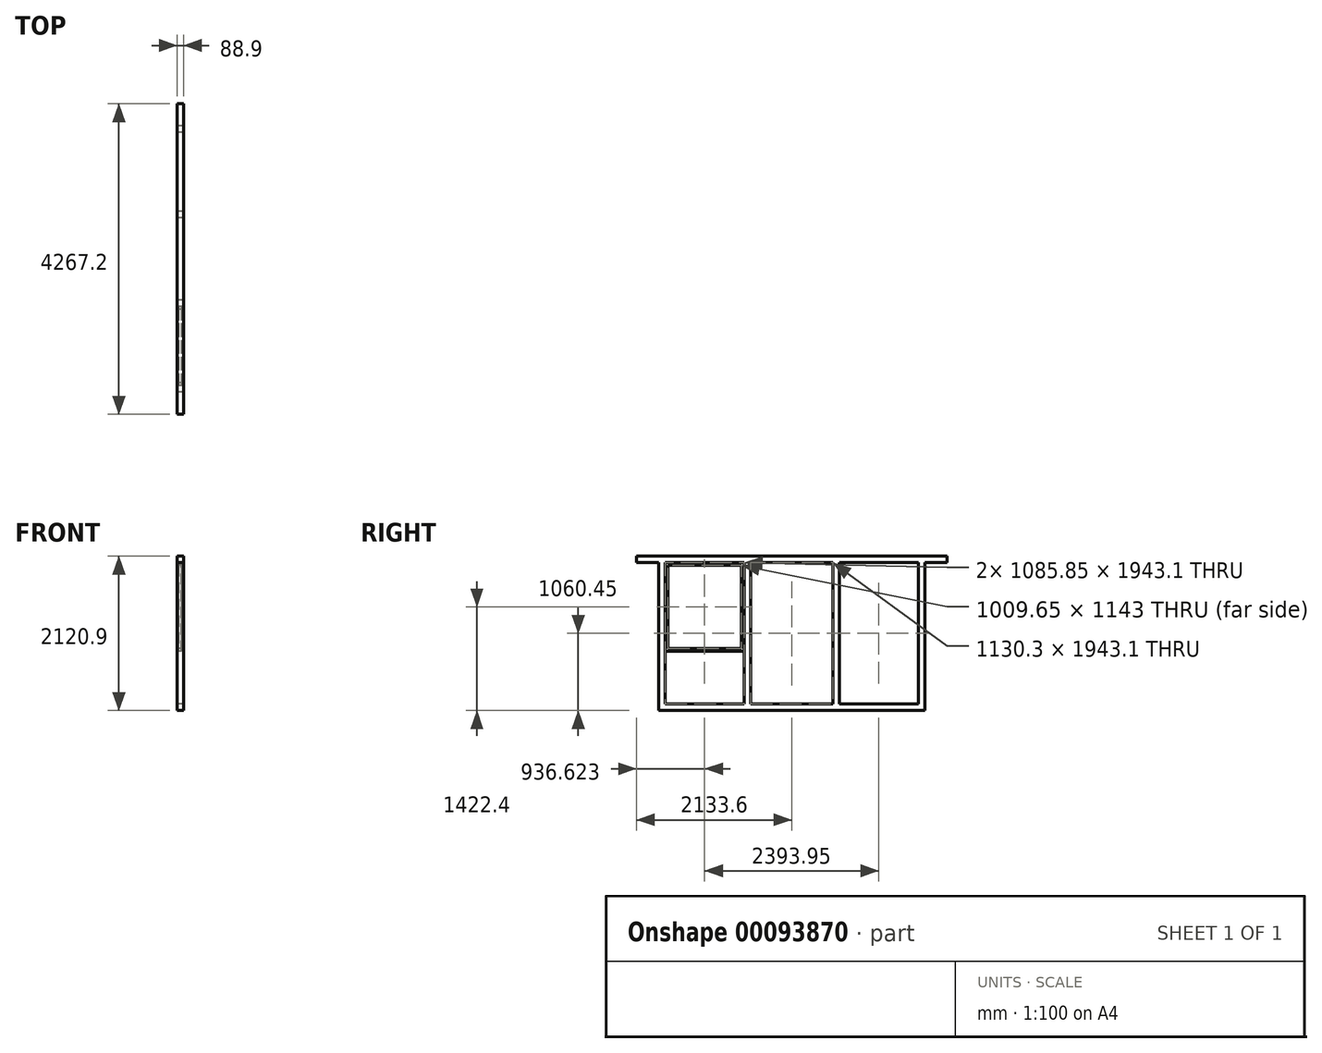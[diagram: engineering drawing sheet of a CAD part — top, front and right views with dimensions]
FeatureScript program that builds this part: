
annotation { "Feature Type Name" : "Feature", "Feature Type Description" : "" }
export const myFeature = defineFeature(function(context is Context, id is Id, definition is map)
    precondition{}
    {
        {
            var Q0;
            Q0=qCreatedBy(makeId("Right.planeOp"),FACE);
            var sketch = newSketch(context, id + "F0", { "sketchPlane" : qUnion([Q0])});
            skLineSegment(sketch, "E0.bottom", {"start": v(-158.68, 2120.9) * mm, "end": v(3498.92, 2120.9) * mm});
            skLineSegment(sketch, "E0.top", {"start": v(-158.68, 0) * mm, "end": v(3498.92, 0) * mm});
            skLineSegment(sketch, "E0.left", {"start": v(-158.68, 2120.9) * mm, "end": v(-158.68, 2032) * mm, "construction": true});
            skLineSegment(sketch, "E0.right", {"start": v(3498.92, 2120.9) * mm, "end": v(3498.92, 2032) * mm, "construction": true});
            skLineSegment(sketch, "E1", {"start": v(1060.52, 2120.9) * mm, "end": v(1060.52, 0) * mm, "construction": true});
            skLineSegment(sketch, "E2", {"start": v(2279.72, 2120.9) * mm, "end": v(2279.72, 0) * mm, "construction": true});
            skLineSegment(sketch, "E3.bottom", {"start": v(-69.78, 2032) * mm, "end": v(1016.07, 2032) * mm});
            skLineSegment(sketch, "E3.top", {"start": v(-69.78, 88.9) * mm, "end": v(1016.07, 88.9) * mm});
            skLineSegment(sketch, "E3.left", {"start": v(-69.78, 2032) * mm, "end": v(-69.78, 88.9) * mm});
            skLineSegment(sketch, "E3.right", {"start": v(1016.07, 2032) * mm, "end": v(1016.07, 88.9) * mm});
            skLineSegment(sketch, "E4.bottom", {"start": v(1104.97, 2032) * mm, "end": v(2235.27, 2032) * mm});
            skLineSegment(sketch, "E4.top", {"start": v(1104.97, 88.9) * mm, "end": v(2235.27, 88.9) * mm});
            skLineSegment(sketch, "E4.left", {"start": v(1104.97, 2032) * mm, "end": v(1104.97, 88.9) * mm});
            skLineSegment(sketch, "E4.right", {"start": v(2235.27, 2032) * mm, "end": v(2235.27, 88.9) * mm});
            skLineSegment(sketch, "E5.bottom", {"start": v(2324.17, 2032) * mm, "end": v(3410.02, 2032) * mm});
            skLineSegment(sketch, "E5.top", {"start": v(2324.17, 88.9) * mm, "end": v(3410.02, 88.9) * mm});
            skLineSegment(sketch, "E5.left", {"start": v(2324.17, 2032) * mm, "end": v(2324.17, 88.9) * mm});
            skLineSegment(sketch, "E5.right", {"start": v(3410.02, 2032) * mm, "end": v(3410.02, 88.9) * mm});
            skLineSegment(sketch, "E6", {"start": v(-158.68, 2120.9) * mm, "end": v(-463.48, 2120.9) * mm});
            skLineSegment(sketch, "E7", {"start": v(-463.48, 2120.9) * mm, "end": v(-463.48, 2032) * mm});
            skLineSegment(sketch, "E8", {"start": v(-463.48, 2032) * mm, "end": v(-158.68, 2032) * mm});
            skLineSegment(sketch, "E9", {"start": v(-158.68, 2032) * mm, "end": v(-158.68, 0) * mm});
            skLineSegment(sketch, "E10", {"start": v(3498.92, 2120.9) * mm, "end": v(3803.72, 2120.9) * mm});
            skLineSegment(sketch, "E11", {"start": v(3803.72, 2120.9) * mm, "end": v(3803.72, 2032) * mm});
            skLineSegment(sketch, "E12", {"start": v(3803.72, 2032) * mm, "end": v(3498.92, 2032) * mm});
            skLineSegment(sketch, "E13", {"start": v(3498.92, 2032) * mm, "end": v(3498.92, 0) * mm});
            skSolve(sketch);
        }
        {
            var Q0;
            Q0 = qSketchRegion(id + "F0", true);
            extrude(context, id + "F1", {"entities" : qUnion([Q0]), "depth" : 88.9 * mm});
        }
        {
            var Q0;
            Q0=makeQuery(id+"F1.opExtrude","CAP_FACE",FACE,{"disambiguationData":[OSD([sQuery(id+"F0.wireOp",EDGE,"E0.bottom"),sQuery(id+"F0.wireOp",EDGE,"E0.top"),sQuery(id+"F0.wireOp",EDGE,"E3.bottom"),sQuery(id+"F0.wireOp",EDGE,"E3.top"),sQuery(id+"F0.wireOp",EDGE,"E3.left"),sQuery(id+"F0.wireOp",EDGE,"E3.right"),sQuery(id+"F0.wireOp",EDGE,"E4.bottom"),sQuery(id+"F0.wireOp",EDGE,"E4.top"),sQuery(id+"F0.wireOp",EDGE,"E4.left"),sQuery(id+"F0.wireOp",EDGE,"E4.right"),sQuery(id+"F0.wireOp",EDGE,"E5.bottom"),sQuery(id+"F0.wireOp",EDGE,"E5.top"),sQuery(id+"F0.wireOp",EDGE,"E5.left"),sQuery(id+"F0.wireOp",EDGE,"E5.right"),sQuery(id+"F0.wireOp",EDGE,"E6"),sQuery(id+"F0.wireOp",EDGE,"E7"),sQuery(id+"F0.wireOp",EDGE,"E8"),sQuery(id+"F0.wireOp",EDGE,"E9"),sQuery(id+"F0.wireOp",EDGE,"E10"),sQuery(id+"F0.wireOp",EDGE,"E11"),sQuery(id+"F0.wireOp",EDGE,"E12"),sQuery(id+"F0.wireOp",EDGE,"E13")])],"isStart":false});
            cPlane(context, id + "F2", {"entities" : qUnion([Q0]), "cplaneType" : CPlaneType.OFFSET, "offset" : 44.45 * mm, "oppositeDirection" : true, "width" : 152.4 * mm, "height" : 152.4 * mm});
        }
        {
            var Q0;
            Q0=qCreatedBy(id+"F2.planeOp",FACE);
            var sketch = newSketch(context, id + "F3", { "sketchPlane" : qUnion([Q0])});
            skLineSegment(sketch, "E14.0", {"start": v(-69.78, 2032) * mm, "end": v(1016.07, 2032) * mm});
            skLineSegment(sketch, "E15.0", {"start": v(1104.97, 2032) * mm, "end": v(2235.27, 2032) * mm, "construction": true});
            skLineSegment(sketch, "E16.0", {"start": v(2324.17, 2032) * mm, "end": v(3410.02, 2032) * mm, "construction": true});
            skLineSegment(sketch, "E17.0", {"start": v(-69.78, 2032) * mm, "end": v(-69.78, 88.9) * mm, "construction": true});
            skLineSegment(sketch, "E18.0", {"start": v(1016.07, 2032) * mm, "end": v(1016.07, 88.9) * mm, "construction": true});
            skLineSegment(sketch, "E19", {"start": v(-69.78, 2032) * mm, "end": v(-69.78, 812.8) * mm});
            skLineSegment(sketch, "E20", {"start": v(-69.78, 812.8) * mm, "end": v(1016.07, 812.8) * mm});
            skLineSegment(sketch, "E21", {"start": v(1016.07, 812.8) * mm, "end": v(1016.07, 2032) * mm});
            skLineSegment(sketch, "E22", {"start": v(1104.97, 812.8) * mm, "end": v(2235.27, 812.8) * mm, "construction": true});
            skLineSegment(sketch, "E23", {"start": v(2235.27, 812.8) * mm, "end": v(2235.27, 2032) * mm, "construction": true});
            skLineSegment(sketch, "E24", {"start": v(2324.17, 812.8) * mm, "end": v(3410.02, 812.8) * mm, "construction": true});
            skSolve(sketch);
        }
        {
            var Q0;
            Q0=makeQuery(id+"F1.opExtrude","SWEPT_FACE",FACE,{"disambiguationData":[OSD([sQuery(id+"F0.wireOp",EDGE,"E3.bottom")])]});
            var sketch = newSketch(context, id + "F4", { "sketchPlane" : qUnion([Q0])});
            skLineSegment(sketch, "E25.bottom", {"start": v(57.15, 69.78) * mm, "end": v(19.05, 69.78) * mm});
            skLineSegment(sketch, "E25.top", {"start": v(57.15, 31.68) * mm, "end": v(19.05, 31.68) * mm});
            skLineSegment(sketch, "E25.left", {"start": v(57.15, 69.78) * mm, "end": v(57.15, 31.68) * mm});
            skLineSegment(sketch, "E25.right", {"start": v(19.05, 69.78) * mm, "end": v(19.05, 31.68) * mm});
            skSolve(sketch);
        }
        {
            var Q0;
            Q0 = qSketchRegion(id + "F4", true);
            var Q1;
            Q1 = qConstructionFilter(qBodyType(qCreatedBy(id + "F3" ,EDGE), BodyType.WIRE), ConstructionObject.NO);
            sweep(context, id + "F5", {"profiles" : qUnion([Q0]), "path" : qUnion([Q1])});
        }
    });
